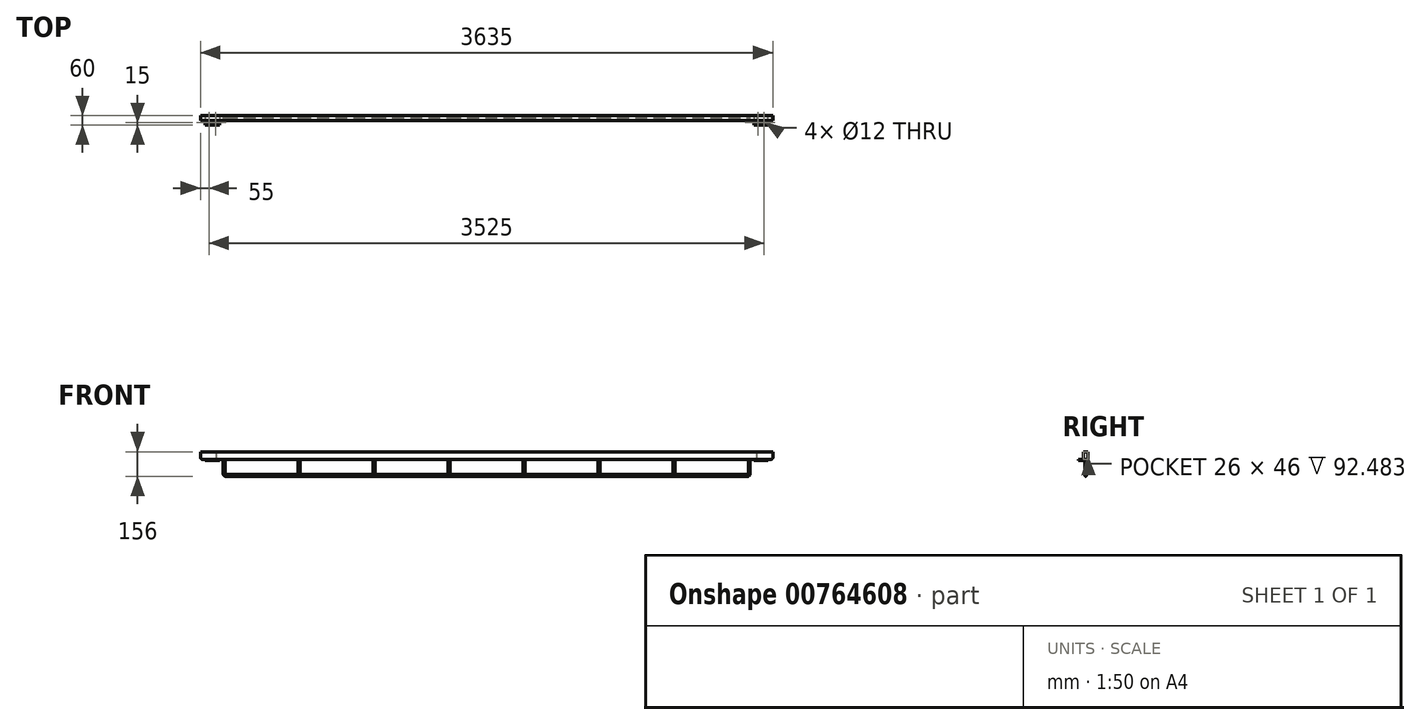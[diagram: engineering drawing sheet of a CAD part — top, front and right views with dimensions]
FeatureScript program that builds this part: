
annotation { "Feature Type Name" : "Feature", "Feature Type Description" : "" }
export const myFeature = defineFeature(function(context is Context, id is Id, definition is map)
    precondition{}
    {
        {
            var Q0;
            Q0=qCreatedBy(makeId("Front.planeOp"),FACE);
            var sketch = newSketch(context, id + "F0", { "sketchPlane" : qUnion([Q0])});
            skLineSegment(sketch, "E0.bottom", {"start": v(1787.5, -25) * mm, "end": v(-1787.5, -25) * mm});
            skLineSegment(sketch, "E0.top", {"start": v(1787.5, 25) * mm, "end": v(-1787.5, 25) * mm});
            skLineSegment(sketch, "E0.left", {"start": v(1787.5, -25) * mm, "end": v(1787.5, 25) * mm});
            skLineSegment(sketch, "E0.right", {"start": v(-1787.5, -25) * mm, "end": v(-1787.5, 25) * mm});
            skPoint(sketch, "E0.middle", {"position": v(0, 0) * mm});
            skSolve(sketch);
        }
        {
            var Q0;
            Q0=qSketchRegion(id+"F0",true);
            extrude(context, id + "F1", {"entities" : qUnion([Q0]), "depth" : 15 * mm, "offsetDistance" : 25 * mm, "hasSecondDirection" : true, "secondDirectionOppositeDirection" : true, "secondDirectionDepth" : 15 * mm});
        }
        {
            var Q0;
            Q0=makeQuery(id+"F1.opExtrude","SWEPT_FACE",FACE,{"disambiguationData":[OSD([sQuery(id+"F0.wireOp",EDGE,"E0.bottom")])]});
            var sketch = newSketch(context, id + "F2", { "sketchPlane" : qUnion([Q0])});
            skLineSegment(sketch, "E1.0", {"start": v(-1787.5, 15) * mm, "end": v(-1787.5, -15) * mm});
            skLineSegment(sketch, "E2.bottom", {"start": v(-1787.5, -15) * mm, "end": v(-1697.5, -15) * mm});
            skLineSegment(sketch, "E2.top", {"start": v(-1787.5, 45) * mm, "end": v(-1697.5, 45) * mm});
            skLineSegment(sketch, "E2.left", {"start": v(-1787.5, -15) * mm, "end": v(-1787.5, 45) * mm});
            skLineSegment(sketch, "E2.right", {"start": v(-1697.5, -15) * mm, "end": v(-1697.5, 45) * mm});
            skSolve(sketch);
        }
        {
            var Q0;
            Q0=qSketchRegion(id+"F2",true);
            extrude(context, id + "F3", {"entities" : qUnion([Q0]), "operationType" : NewBodyOperationType.ADD, "depth" : 5 * mm, "offsetDistance" : 25 * mm});
        }
        {
            var Q0;
            Q0=makeQuery(id+"F1.opExtrude","SWEPT_FACE",FACE,{"disambiguationData":[OSD([sQuery(id+"F0.wireOp",EDGE,"E0.bottom")])]});
            var sketch = newSketch(context, id + "F4", { "sketchPlane" : qUnion([Q0])});
            skLineSegment(sketch, "E3.0", {"start": v(1787.5, 15) * mm, "end": v(1787.5, -15) * mm});
            skLineSegment(sketch, "E4.bottom", {"start": v(1787.5, -15) * mm, "end": v(1697.5, -15) * mm});
            skLineSegment(sketch, "E4.top", {"start": v(1787.5, 45) * mm, "end": v(1697.5, 45) * mm});
            skLineSegment(sketch, "E4.left", {"start": v(1787.5, -15) * mm, "end": v(1787.5, 45) * mm});
            skLineSegment(sketch, "E4.right", {"start": v(1697.5, -15) * mm, "end": v(1697.5, 45) * mm});
            skSolve(sketch);
        }
        {
            var Q0;
            Q0=qSketchRegion(id+"F4",true);
            extrude(context, id + "F5", {"entities" : qUnion([Q0]), "operationType" : NewBodyOperationType.ADD, "depth" : 5 * mm, "offsetDistance" : 25 * mm});
        }
        {
            var Q0;
            Q0=makeQuery(id+"F3.opExtrude","CAP_FACE",FACE,{"disambiguationData":[OSD([sQuery(id+"F2.wireOp",EDGE,"E2.bottom"),sQuery(id+"F2.wireOp",EDGE,"E2.top"),sQuery(id+"F2.wireOp",EDGE,"E2.left"),sQuery(id+"F2.wireOp",EDGE,"E2.right")])],"isStart":false});
            var sketch = newSketch(context, id + "F6", { "sketchPlane" : qUnion([Q0])});
            skCircle(sketch, "E5.0", {"center": v(-935, 30) * mm, "radius": 6 * mm});
            skCircle(sketch, "E6.0", {"center": v(-975, 30) * mm, "radius": 6 * mm});
            skSolve(sketch);
        }
        {
            var Q0;
            Q0=qSketchRegion(id+"F6",true);
            var Q1;
            Q1=makeQuery(id+"F3.opExtrude","CAP_FACE",FACE,{"disambiguationData":[OSD([sQuery(id+"F2.wireOp",EDGE,"E2.bottom"),sQuery(id+"F2.wireOp",EDGE,"E2.top"),sQuery(id+"F2.wireOp",EDGE,"E2.left"),sQuery(id+"F2.wireOp",EDGE,"E2.right")])],"isStart":true});
            extrude(context, id + "F7", {"entities" : qUnion([Q0]), "operationType" : NewBodyOperationType.REMOVE, "endBound" : BoundingType.UP_TO_SURFACE, "oppositeDirection" : true, "depth" : 25 * mm, "endBoundEntityFace" : qUnion([Q1]), "offsetDistance" : 25 * mm});
        }
        {
            var Q0;
            Q0=makeQuery(id+"F5.opExtrude","CAP_FACE",FACE,{"disambiguationData":[OSD([sQuery(id+"F4.wireOp",EDGE,"E4.bottom"),sQuery(id+"F4.wireOp",EDGE,"E4.top"),sQuery(id+"F4.wireOp",EDGE,"E4.left"),sQuery(id+"F4.wireOp",EDGE,"E4.right")])],"isStart":false});
            var sketch = newSketch(context, id + "F8", { "sketchPlane" : qUnion([Q0])});
            skCircle(sketch, "E7.0", {"center": v(1762.5, 30) * mm, "radius": 6 * mm});
            skCircle(sketch, "E8.0", {"center": v(1722.5, 30) * mm, "radius": 6 * mm});
            skSolve(sketch);
        }
        {
            var Q0;
            Q0=qSketchRegion(id+"F8",true);
            var Q1;
            Q1=makeQuery(id+"F5.opExtrude","CAP_FACE",FACE,{"disambiguationData":[OSD([sQuery(id+"F4.wireOp",EDGE,"E4.bottom"),sQuery(id+"F4.wireOp",EDGE,"E4.top"),sQuery(id+"F4.wireOp",EDGE,"E4.left"),sQuery(id+"F4.wireOp",EDGE,"E4.right")])],"isStart":true});
            extrude(context, id + "F9", {"entities" : qUnion([Q0]), "operationType" : NewBodyOperationType.REMOVE, "endBound" : BoundingType.UP_TO_SURFACE, "oppositeDirection" : true, "depth" : 25 * mm, "endBoundEntityFace" : qUnion([Q1]), "offsetDistance" : 25 * mm});
        }
        {
            var Q0;
            Q0=makeQuery(id+"F1.opExtrude","SWEPT_FACE",FACE,{"disambiguationData":[OSD([sQuery(id+"F0.wireOp",EDGE,"E0.bottom")])]});
            var sketch = newSketch(context, id + "F10", { "sketchPlane" : qUnion([Q0])});
            skLineSegment(sketch, "E9", {"start": v(-1697.5, -15) * mm, "end": v(-1667.5, -15) * mm, "construction": true});
            skLineSegment(sketch, "E10", {"start": v(-1667.5, -15) * mm, "end": v(-1667.5, 15) * mm, "construction": true});
            skCircle(sketch, "E11", {"center": v(-1667.5, 0) * mm, "radius": 6 * mm});
            skLineSegment(sketch, "E12", {"start": v(1697.5, -15) * mm, "end": v(1667.5, -15) * mm, "construction": true});
            skLineSegment(sketch, "E13", {"start": v(1667.5, -15) * mm, "end": v(1667.5, 15) * mm, "construction": true});
            skCircle(sketch, "E14", {"center": v(1667.5, 0) * mm, "radius": 6 * mm});
            skLineSegment(sketch, "E15", {"start": v(1667.5, 0) * mm, "end": v(1191.07, 0) * mm});
            skLineSegment(sketch, "E16", {"start": v(1191.07, 0) * mm, "end": v(714.64, 0) * mm});
            skLineSegment(sketch, "E17", {"start": v(714.64, 0) * mm, "end": v(238.21, 0) * mm});
            skLineSegment(sketch, "E18", {"start": v(238.21, 0) * mm, "end": v(-238.21, 0) * mm});
            skLineSegment(sketch, "E19", {"start": v(-238.21, 0) * mm, "end": v(-714.64, 0) * mm});
            skLineSegment(sketch, "E20", {"start": v(-714.64, 0) * mm, "end": v(-1191.07, 0) * mm});
            skLineSegment(sketch, "E21", {"start": v(-1667.5, 0) * mm, "end": v(-1191.07, 0) * mm});
            skCircle(sketch, "E22", {"center": v(-1191.07, 0) * mm, "radius": 6 * mm});
            skCircle(sketch, "E23", {"center": v(-714.64, 0) * mm, "radius": 6 * mm});
            skCircle(sketch, "E24", {"center": v(-238.21, 0) * mm, "radius": 6 * mm});
            skCircle(sketch, "E25", {"center": v(238.21, 0) * mm, "radius": 6 * mm});
            skCircle(sketch, "E26", {"center": v(714.64, 0) * mm, "radius": 6 * mm});
            skCircle(sketch, "E27", {"center": v(1191.07, 0) * mm, "radius": 6 * mm});
            skSolve(sketch);
        }
        {
            var Q0;
            Q0=qCreatedBy(makeId("Front.planeOp"),FACE);
            var sketch = newSketch(context, id + "F11", { "sketchPlane" : qUnion([Q0])});
            skLineSegment(sketch, "E28.0", {"start": v(-1667.5, -25) * mm, "end": v(-1191.07, -25) * mm});
            skLineSegment(sketch, "E29.0", {"start": v(-714.64, -25) * mm, "end": v(-1191.07, -25) * mm});
            skLineSegment(sketch, "E30.0", {"start": v(-238.21, -25) * mm, "end": v(-714.64, -25) * mm});
            skLineSegment(sketch, "E31.0", {"start": v(238.21, -25) * mm, "end": v(-238.21, -25) * mm});
            skLineSegment(sketch, "E32.0", {"start": v(714.64, -25) * mm, "end": v(238.21, -25) * mm});
            skLineSegment(sketch, "E33.0", {"start": v(1191.07, -25) * mm, "end": v(714.64, -25) * mm});
            skLineSegment(sketch, "E34.0", {"start": v(1667.5, -25) * mm, "end": v(1191.07, -25) * mm});
            skLineSegment(sketch, "E35", {"start": v(1667.5, -25) * mm, "end": v(1667.5, -115) * mm});
            skLineSegment(sketch, "E36", {"start": v(1667.5, -115) * mm, "end": v(1657.5, -115) * mm});
            skArc(sketch, "E37", {"start": v(1657.5, -125) * mm, "mid": v(1664.57, -122.07) * mm, "end": v(1667.5, -115) * mm});
            skLineSegment(sketch, "E38", {"start": v(1657.5, -115) * mm, "end": v(1657.5, -125) * mm, "construction": true});
            skLineSegment(sketch, "E39", {"start": v(-1667.5, -25) * mm, "end": v(-1667.5, -115) * mm});
            skLineSegment(sketch, "E40", {"start": v(-1667.5, -115) * mm, "end": v(-1657.5, -115) * mm});
            skArc(sketch, "E41", {"start": v(-1667.5, -115) * mm, "mid": v(-1664.57, -122.07) * mm, "end": v(-1657.5, -125) * mm});
            skLineSegment(sketch, "E42", {"start": v(-1657.5, -115) * mm, "end": v(-1657.5, -125) * mm, "construction": true});
            skLineSegment(sketch, "E43", {"start": v(-1657.5, -125) * mm, "end": v(1657.5, -125) * mm});
            skLineSegment(sketch, "E44", {"start": v(1191.07, -25) * mm, "end": v(1191.07, -125) * mm});
            skLineSegment(sketch, "E45", {"start": v(714.64, -25) * mm, "end": v(714.64, -125) * mm});
            skLineSegment(sketch, "E46", {"start": v(238.21, -25) * mm, "end": v(238.21, -125) * mm});
            skLineSegment(sketch, "E47", {"start": v(-238.21, -25) * mm, "end": v(-238.21, -125) * mm});
            skLineSegment(sketch, "E48", {"start": v(-714.64, -25) * mm, "end": v(-714.64, -125) * mm});
            skLineSegment(sketch, "E49", {"start": v(-1191.07, -25) * mm, "end": v(-1191.07, -125) * mm});
            skSolve(sketch);
        }
        {
            var Q0;
            Q0=makeQuery(id+"F10.imprint","IMPRINT",FACE,{"disambiguationData":[TD([[makeQuery(id+"F10.imprint","IMPRINT",EDGE,{"derivedFrom":sQuery(id+"F10.wireOp",EDGE,"E11")}),1.0]])]});
            var Q1;
            Q1=sQuery(id+"F11.wireOp",EDGE,"E39");
            var Q2;
            Q2=sQuery(id+"F11.wireOp",EDGE,"E41");
            var Q3;
            Q3=sQuery(id+"F11.wireOp",EDGE,"E43");
            var Q4;
            Q4=sQuery(id+"F11.wireOp",EDGE,"E37");
            var Q5;
            Q5=sQuery(id+"F11.wireOp",EDGE,"E35");
            sweep(context, id + "F12", {"operationType" : NewBodyOperationType.ADD, "profiles" : qUnion([Q0]), "path" : qUnion([Q1, Q2, Q3, Q4, Q5])});
        }
        {
            var Q0;
            {var subQ0=sQuery(id+"F10.wireOp",EDGE,"E21");var subQ1=sQuery(id+"F10.wireOp",EDGE,"E20");var subQ2=makeQuery(id+"F10.imprint","INTERSECT",VERTEX,{"derivedFrom":[subQ1,subQ0]});Q0=makeQuery(id+"F10.imprint","IMPRINT",FACE,{"disambiguationData":[TD([[makeQuery(id+"F10.imprint","IMPRINT",EDGE,{"disambiguationData":[TD([[subQ2,1.0]])],"derivedFrom":subQ1}),1.0]])]});}
            var Q1;
            {var subQ0=sQuery(id+"F10.wireOp",EDGE,"E21");var subQ1=sQuery(id+"F10.wireOp",EDGE,"E20");var subQ2=makeQuery(id+"F10.imprint","INTERSECT",VERTEX,{"derivedFrom":[subQ1,subQ0]});Q1=makeQuery(id+"F10.imprint","IMPRINT",FACE,{"disambiguationData":[TD([[makeQuery(id+"F10.imprint","IMPRINT",EDGE,{"disambiguationData":[TD([[subQ2,1.0]])],"derivedFrom":subQ1}),-1.0]])]});}
            var Q2;
            Q2=sQuery(id+"F11.wireOp",EDGE,"E49");
            sweep(context, id + "F13", {"operationType" : NewBodyOperationType.ADD, "profiles" : qUnion([Q0, Q1]), "path" : qUnion([Q2])});
        }
        {
            var Q0;
            {var subQ0=sQuery(id+"F10.wireOp",EDGE,"E20");var subQ1=sQuery(id+"F10.wireOp",EDGE,"E19");var subQ2=makeQuery(id+"F10.imprint","INTERSECT",VERTEX,{"derivedFrom":[subQ1,subQ0]});Q0=makeQuery(id+"F10.imprint","IMPRINT",FACE,{"disambiguationData":[TD([[makeQuery(id+"F10.imprint","IMPRINT",EDGE,{"disambiguationData":[TD([[subQ2,1.0]])],"derivedFrom":subQ1}),-1.0]])]});}
            var Q1;
            {var subQ0=sQuery(id+"F10.wireOp",EDGE,"E20");var subQ1=sQuery(id+"F10.wireOp",EDGE,"E19");var subQ2=makeQuery(id+"F10.imprint","INTERSECT",VERTEX,{"derivedFrom":[subQ1,subQ0]});Q1=makeQuery(id+"F10.imprint","IMPRINT",FACE,{"disambiguationData":[TD([[makeQuery(id+"F10.imprint","IMPRINT",EDGE,{"disambiguationData":[TD([[subQ2,1.0]])],"derivedFrom":subQ1}),1.0]])]});}
            var Q2;
            Q2=sQuery(id+"F11.wireOp",EDGE,"E48");
            sweep(context, id + "F14", {"operationType" : NewBodyOperationType.ADD, "profiles" : qUnion([Q0, Q1]), "path" : qUnion([Q2])});
        }
        {
            var Q0;
            {var subQ0=sQuery(id+"F10.wireOp",EDGE,"E19");var subQ1=sQuery(id+"F10.wireOp",EDGE,"E18");var subQ2=makeQuery(id+"F10.imprint","INTERSECT",VERTEX,{"derivedFrom":[subQ1,subQ0]});Q0=makeQuery(id+"F10.imprint","IMPRINT",FACE,{"disambiguationData":[TD([[makeQuery(id+"F10.imprint","IMPRINT",EDGE,{"disambiguationData":[TD([[subQ2,1.0]])],"derivedFrom":subQ1}),-1.0]])]});}
            var Q1;
            {var subQ0=sQuery(id+"F10.wireOp",EDGE,"E19");var subQ1=sQuery(id+"F10.wireOp",EDGE,"E18");var subQ2=makeQuery(id+"F10.imprint","INTERSECT",VERTEX,{"derivedFrom":[subQ1,subQ0]});Q1=makeQuery(id+"F10.imprint","IMPRINT",FACE,{"disambiguationData":[TD([[makeQuery(id+"F10.imprint","IMPRINT",EDGE,{"disambiguationData":[TD([[subQ2,1.0]])],"derivedFrom":subQ1}),1.0]])]});}
            var Q2;
            Q2=sQuery(id+"F11.wireOp",EDGE,"E47");
            sweep(context, id + "F15", {"operationType" : NewBodyOperationType.ADD, "profiles" : qUnion([Q0, Q1]), "path" : qUnion([Q2])});
        }
        {
            var Q0;
            Q0=makeQuery(id+"F10.imprint","IMPRINT",FACE,{"disambiguationData":[TD([[makeQuery(id+"F10.imprint","IMPRINT",EDGE,{"derivedFrom":sQuery(id+"F10.wireOp",EDGE,"E11")}),1.0]])]});
            var Q1;
            Q1=sQuery(id+"F11.wireOp",EDGE,"E39");
            var Q2;
            Q2=sQuery(id+"F11.wireOp",EDGE,"E41");
            var Q3;
            Q3=sQuery(id+"F11.wireOp",EDGE,"E43");
            var Q4;
            Q4=sQuery(id+"F11.wireOp",EDGE,"E37");
            sweep(context, id + "F16", {"operationType" : NewBodyOperationType.ADD, "profiles" : qUnion([Q0]), "path" : qUnion([Q1, Q2, Q3, Q4])});
        }
        {
            var Q0;
            {var subQ0=sQuery(id+"F10.wireOp",EDGE,"E18");var subQ1=sQuery(id+"F10.wireOp",EDGE,"E17");var subQ2=makeQuery(id+"F10.imprint","INTERSECT",VERTEX,{"derivedFrom":[subQ1,subQ0]});Q0=makeQuery(id+"F10.imprint","IMPRINT",FACE,{"disambiguationData":[TD([[makeQuery(id+"F10.imprint","IMPRINT",EDGE,{"disambiguationData":[TD([[subQ2,1.0]])],"derivedFrom":subQ1}),-1.0]])]});}
            var Q1;
            {var subQ0=sQuery(id+"F10.wireOp",EDGE,"E18");var subQ1=sQuery(id+"F10.wireOp",EDGE,"E17");var subQ2=makeQuery(id+"F10.imprint","INTERSECT",VERTEX,{"derivedFrom":[subQ1,subQ0]});Q1=makeQuery(id+"F10.imprint","IMPRINT",FACE,{"disambiguationData":[TD([[makeQuery(id+"F10.imprint","IMPRINT",EDGE,{"disambiguationData":[TD([[subQ2,1.0]])],"derivedFrom":subQ1}),1.0]])]});}
            var Q2;
            Q2=sQuery(id+"F11.wireOp",EDGE,"E46");
            sweep(context, id + "F17", {"operationType" : NewBodyOperationType.ADD, "profiles" : qUnion([Q0, Q1]), "path" : qUnion([Q2])});
        }
        {
            var Q0;
            {var subQ0=sQuery(id+"F10.wireOp",EDGE,"E17");var subQ1=sQuery(id+"F10.wireOp",EDGE,"E16");var subQ2=makeQuery(id+"F10.imprint","INTERSECT",VERTEX,{"derivedFrom":[subQ1,subQ0]});Q0=makeQuery(id+"F10.imprint","IMPRINT",FACE,{"disambiguationData":[TD([[makeQuery(id+"F10.imprint","IMPRINT",EDGE,{"disambiguationData":[TD([[subQ2,1.0]])],"derivedFrom":subQ1}),-1.0]])]});}
            var Q1;
            {var subQ0=sQuery(id+"F10.wireOp",EDGE,"E17");var subQ1=sQuery(id+"F10.wireOp",EDGE,"E16");var subQ2=makeQuery(id+"F10.imprint","INTERSECT",VERTEX,{"derivedFrom":[subQ1,subQ0]});Q1=makeQuery(id+"F10.imprint","IMPRINT",FACE,{"disambiguationData":[TD([[makeQuery(id+"F10.imprint","IMPRINT",EDGE,{"disambiguationData":[TD([[subQ2,1.0]])],"derivedFrom":subQ1}),1.0]])]});}
            var Q2;
            Q2=sQuery(id+"F11.wireOp",EDGE,"E45");
            sweep(context, id + "F18", {"operationType" : NewBodyOperationType.ADD, "profiles" : qUnion([Q0, Q1]), "path" : qUnion([Q2])});
        }
        {
            var Q0;
            {var subQ0=sQuery(id+"F10.wireOp",EDGE,"E16");var subQ1=sQuery(id+"F10.wireOp",EDGE,"E15");var subQ2=makeQuery(id+"F10.imprint","INTERSECT",VERTEX,{"derivedFrom":[subQ1,subQ0]});Q0=makeQuery(id+"F10.imprint","IMPRINT",FACE,{"disambiguationData":[TD([[makeQuery(id+"F10.imprint","IMPRINT",EDGE,{"disambiguationData":[TD([[subQ2,1.0]])],"derivedFrom":subQ1}),1.0]])]});}
            var Q1;
            {var subQ0=sQuery(id+"F10.wireOp",EDGE,"E16");var subQ1=sQuery(id+"F10.wireOp",EDGE,"E15");var subQ2=makeQuery(id+"F10.imprint","INTERSECT",VERTEX,{"derivedFrom":[subQ1,subQ0]});Q1=makeQuery(id+"F10.imprint","IMPRINT",FACE,{"disambiguationData":[TD([[makeQuery(id+"F10.imprint","IMPRINT",EDGE,{"disambiguationData":[TD([[subQ2,1.0]])],"derivedFrom":subQ1}),-1.0]])]});}
            var Q2;
            Q2=sQuery(id+"F11.wireOp",EDGE,"E44");
            sweep(context, id + "F19", {"operationType" : NewBodyOperationType.ADD, "profiles" : qUnion([Q0, Q1]), "path" : qUnion([Q2])});
        }
        {
            var Q0;
            Q0=makeQuery(id+"F3.opExtrude","CAP_FACE",FACE,{"disambiguationData":[OSD([sQuery(id+"F2.wireOp",EDGE,"E2.bottom"),sQuery(id+"F2.wireOp",EDGE,"E2.top"),sQuery(id+"F2.wireOp",EDGE,"E2.left"),sQuery(id+"F2.wireOp",EDGE,"E2.right")])],"isStart":false});
            var sketch = newSketch(context, id + "F20", { "sketchPlane" : qUnion([Q0])});
            skLineSegment(sketch, "E50.bottom", {"start": v(-1787.5, 45) * mm, "end": v(-1762.5, 45) * mm, "construction": true});
            skLineSegment(sketch, "E50.top", {"start": v(-1787.5, 30) * mm, "end": v(-1762.5, 30) * mm});
            skLineSegment(sketch, "E50.left", {"start": v(-1787.5, 45) * mm, "end": v(-1787.5, 30) * mm});
            skLineSegment(sketch, "E50.right", {"start": v(-1762.5, 45) * mm, "end": v(-1762.5, 30) * mm});
            skLineSegment(sketch, "E51", {"start": v(-1762.5, 30) * mm, "end": v(-1722.5, 30) * mm});
            skCircle(sketch, "E52", {"center": v(-1762.5, 30) * mm, "radius": 6 * mm});
            skCircle(sketch, "E53", {"center": v(-1722.5, 30) * mm, "radius": 6 * mm});
            skSolve(sketch);
        }
        {
            var Q0;
            Q0=qSketchRegion(id+"F20",true);
            extrude(context, id + "F21", {"entities" : qUnion([Q0]), "operationType" : NewBodyOperationType.REMOVE, "endBound" : BoundingType.UP_TO_NEXT, "oppositeDirection" : true, "depth" : 25 * mm, "offsetDistance" : 25 * mm});
        }
        {
            var Q0;
            Q0=makeQuery(id+"F5.boolean.opBoolean","MERGE",FACE,{"derivedFrom":[makeQuery(id+"F1.opExtrude","SWEPT_FACE",FACE,{"disambiguationData":[OSD([sQuery(id+"F0.wireOp",EDGE,"E0.left")])]}),makeQuery(id+"F5.opExtrude","SWEPT_FACE",FACE,{"disambiguationData":[OSD([sQuery(id+"F4.wireOp",EDGE,"E4.left")])]})]});
            var sketch = newSketch(context, id + "F22", { "sketchPlane" : qUnion([Q0])});
            skLineSegment(sketch, "E54.bottom", {"start": v(-15, 25) * mm, "end": v(15, 25) * mm});
            skLineSegment(sketch, "E54.top", {"start": v(-15, -25) * mm, "end": v(15, -25) * mm});
            skLineSegment(sketch, "E54.left", {"start": v(-15, 25) * mm, "end": v(-15, -25) * mm});
            skLineSegment(sketch, "E54.right", {"start": v(15, 25) * mm, "end": v(15, -25) * mm});
            skSolve(sketch);
        }
        {
            var Q0;
            Q0=qSketchRegion(id+"F22",true);
            extrude(context, id + "F23", {"entities" : qUnion([Q0]), "operationType" : NewBodyOperationType.ADD, "depth" : 30 * mm, "offsetDistance" : 25 * mm});
        }
        {
            var Q0;
            Q0=makeQuery(id+"F23.opExtrude","CAP_EDGE",EDGE,{"disambiguationData":[OSD([sQuery(id+"F22.wireOp",EDGE,"E54.top")])],"isStart":false});
            fillet(context, id + "F24", {"entities" : qUnion([Q0]), "radius" : 15 * mm, "tangentPropagation" : true, "allowEdgeOverflow" : false});
        }
        {
            var Q0;
            Q0=makeQuery(id+"F23.opExtrude","CAP_FACE",FACE,{"disambiguationData":[OSD([sQuery(id+"F22.wireOp",EDGE,"E54.bottom"),sQuery(id+"F22.wireOp",EDGE,"E54.top"),sQuery(id+"F22.wireOp",EDGE,"E54.left"),sQuery(id+"F22.wireOp",EDGE,"E54.right")])],"isStart":false});
            var sketch = newSketch(context, id + "F25", { "sketchPlane" : qUnion([Q0])});
            skLineSegment(sketch, "E55.bottom", {"start": v(-15, 25) * mm, "end": v(15, 25) * mm});
            skLineSegment(sketch, "E55.top", {"start": v(-15, -25) * mm, "end": v(15, -25) * mm});
            skLineSegment(sketch, "E55.left", {"start": v(-15, 25) * mm, "end": v(-15, -25) * mm});
            skLineSegment(sketch, "E55.right", {"start": v(15, 25) * mm, "end": v(15, -25) * mm});
            skLineSegment(sketch, "E56", {"start": v(-15, -25) * mm, "end": v(15, 25) * mm, "construction": true});
            skLineSegment(sketch, "E57.bottom", {"start": v(13, -23) * mm, "end": v(-13, -23) * mm});
            skLineSegment(sketch, "E57.top", {"start": v(13, 23) * mm, "end": v(-13, 23) * mm});
            skLineSegment(sketch, "E57.left", {"start": v(13, -23) * mm, "end": v(13, 23) * mm});
            skLineSegment(sketch, "E57.right", {"start": v(-13, -23) * mm, "end": v(-13, 23) * mm});
            skPoint(sketch, "E57.middle", {"position": v(0, 0) * mm});
            skSolve(sketch);
        }
        {
            var Q0;
            {var subQ0=sQuery(id+"F25.wireOp",EDGE,"E57.bottom");Q0=makeQuery(id+"F25.imprint","IMPRINT",FACE,{"disambiguationData":[TD([[makeQuery(id+"F25.imprint","IMPRINT",EDGE,{"derivedFrom":subQ0}),-1.0]])]});}
            var Q1;
            {var subQ0=sQuery(id+"F25.wireOp",EDGE,"E57.top");Q1=makeQuery(id+"F25.imprint","IMPRINT",FACE,{"disambiguationData":[TD([[makeQuery(id+"F25.imprint","IMPRINT",EDGE,{"derivedFrom":subQ0}),1.0]])]});}
            extrude(context, id + "F26", {"entities" : qUnion([Q0, Q1]), "operationType" : NewBodyOperationType.REMOVE, "oppositeDirection" : true, "depth" : 100 * mm, "offsetDistance" : 25 * mm});
        }
        {
            var Q0;
            Q0=makeQuery(id+"F3.boolean.opBoolean","MERGE",FACE,{"derivedFrom":[makeQuery(id+"F1.opExtrude","SWEPT_FACE",FACE,{"disambiguationData":[OSD([sQuery(id+"F0.wireOp",EDGE,"E0.right")])]}),makeQuery(id+"F3.opExtrude","SWEPT_FACE",FACE,{"disambiguationData":[OSD([sQuery(id+"F2.wireOp",EDGE,"E2.left")])]})]});
            var sketch = newSketch(context, id + "F27", { "sketchPlane" : qUnion([Q0])});
            skLineSegment(sketch, "E58.bottom", {"start": v(-15, 25) * mm, "end": v(15, 25) * mm});
            skLineSegment(sketch, "E58.top", {"start": v(-15, -25) * mm, "end": v(15, -25) * mm});
            skLineSegment(sketch, "E58.left", {"start": v(-15, 25) * mm, "end": v(-15, -25) * mm});
            skLineSegment(sketch, "E58.right", {"start": v(15, 25) * mm, "end": v(15, -25) * mm});
            skSolve(sketch);
        }
        {
            var Q0;
            Q0=qSketchRegion(id+"F27",true);
            extrude(context, id + "F28", {"entities" : qUnion([Q0]), "operationType" : NewBodyOperationType.ADD, "depth" : 30 * mm, "offsetDistance" : 25 * mm});
        }
        {
            var Q0;
            Q0=makeQuery(id+"F28.opExtrude","CAP_FACE",FACE,{"disambiguationData":[OSD([sQuery(id+"F27.wireOp",EDGE,"E58.bottom"),sQuery(id+"F27.wireOp",EDGE,"E58.top"),sQuery(id+"F27.wireOp",EDGE,"E58.left"),sQuery(id+"F27.wireOp",EDGE,"E58.right")])],"isStart":false});
            var sketch = newSketch(context, id + "F29", { "sketchPlane" : qUnion([Q0])});
            skLineSegment(sketch, "E59.bottom", {"start": v(-15, 25) * mm, "end": v(15, 25) * mm});
            skLineSegment(sketch, "E59.top", {"start": v(-15, -25) * mm, "end": v(15, -25) * mm});
            skLineSegment(sketch, "E59.left", {"start": v(-15, 25) * mm, "end": v(-15, -25) * mm});
            skLineSegment(sketch, "E59.right", {"start": v(15, 25) * mm, "end": v(15, -25) * mm});
            skLineSegment(sketch, "E60", {"start": v(15, -25) * mm, "end": v(-15, 25) * mm, "construction": true});
            skLineSegment(sketch, "E61.bottom", {"start": v(13, 23) * mm, "end": v(-13, 23) * mm});
            skLineSegment(sketch, "E61.top", {"start": v(13, -23) * mm, "end": v(-13, -23) * mm});
            skLineSegment(sketch, "E61.left", {"start": v(13, 23) * mm, "end": v(13, -23) * mm});
            skLineSegment(sketch, "E61.right", {"start": v(-13, 23) * mm, "end": v(-13, -23) * mm});
            skPoint(sketch, "E61.middle", {"position": v(0, 0) * mm});
            skSolve(sketch);
        }
        {
            var Q0;
            Q0=makeQuery(id+"F29.imprint","IMPRINT",FACE,{"disambiguationData":[TD([[makeQuery(id+"F29.imprint","IMPRINT",EDGE,{"derivedFrom":sQuery(id+"F29.wireOp",EDGE,"E61.bottom")}),1.0]])]});
            extrude(context, id + "F30", {"entities" : qUnion([Q0]), "operationType" : NewBodyOperationType.REMOVE, "oppositeDirection" : true, "depth" : 100 * mm, "offsetDistance" : 25 * mm});
        }
        {
            var Q0;
            Q0=makeQuery(id+"F28.opExtrude","CAP_EDGE",EDGE,{"disambiguationData":[OSD([sQuery(id+"F27.wireOp",EDGE,"E58.top")])],"isStart":false});
            fillet(context, id + "F31", {"entities" : qUnion([Q0]), "radius" : 15 * mm, "tangentPropagation" : true, "allowEdgeOverflow" : false});
        }
    });
